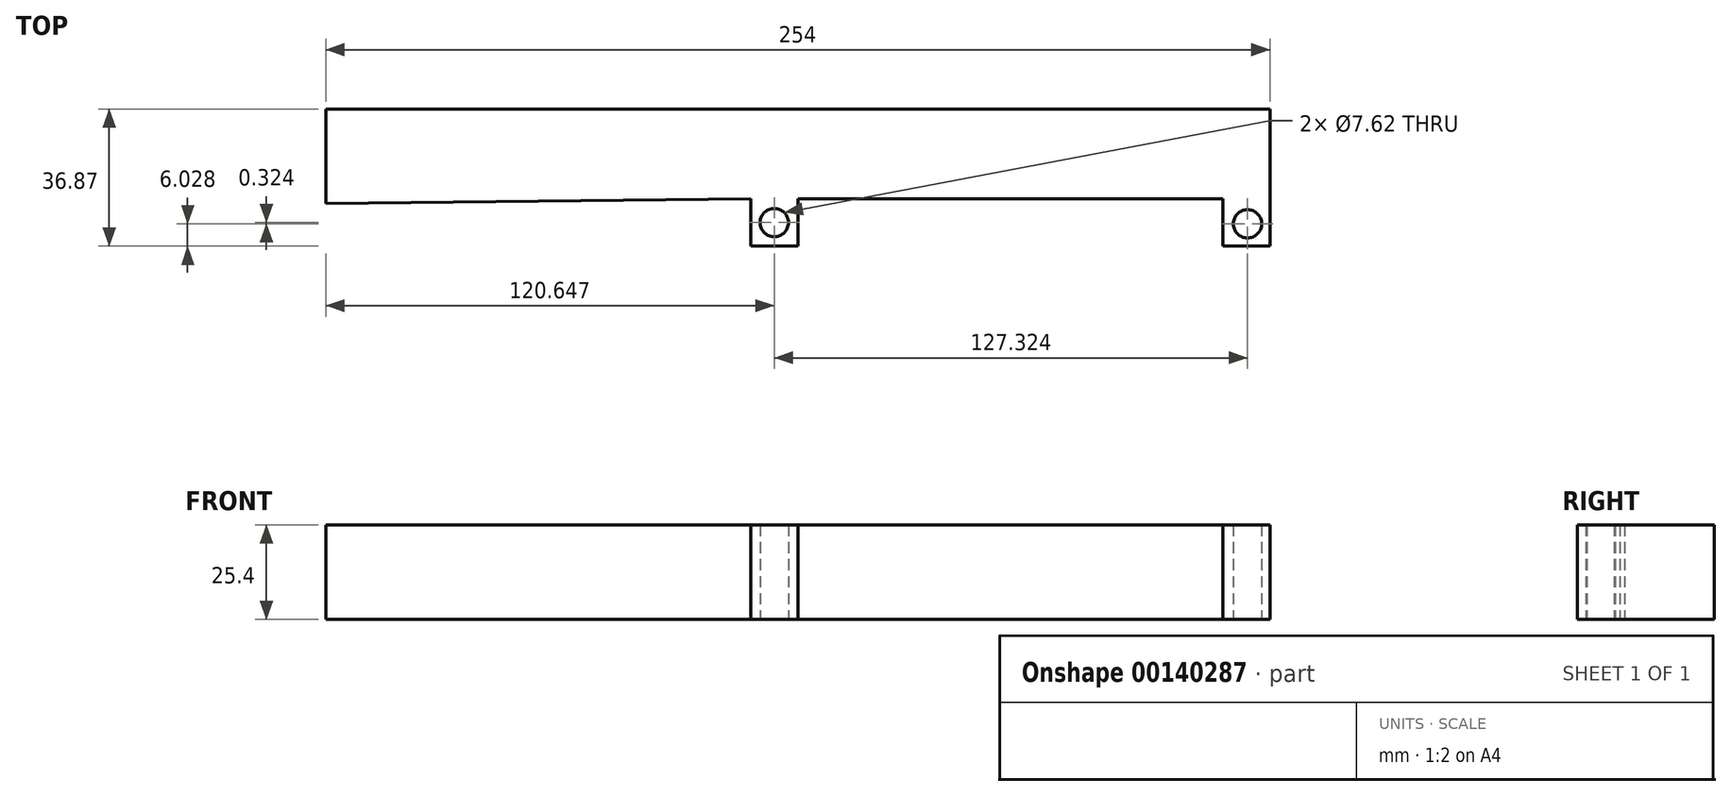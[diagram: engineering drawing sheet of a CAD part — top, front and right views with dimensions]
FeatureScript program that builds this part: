
annotation { "Feature Type Name" : "Feature", "Feature Type Description" : "" }
export const myFeature = defineFeature(function(context is Context, id is Id, definition is map)
    precondition{}
    {
        {
            var Q0;
            Q0=qCreatedBy(makeId("Top.planeOp"),FACE);
            var sketch = newSketch(context, id + "F0", { "sketchPlane" : qUnion([Q0])});
            skLineSegment(sketch, "E0.bottom", {"start": v(-370.92, 72.32) * mm, "end": v(-116.92, 72.32) * mm});
            skLineSegment(sketch, "E0.left", {"start": v(-370.92, 72.32) * mm, "end": v(-370.92, 46.92) * mm});
            skLineSegment(sketch, "E0.right", {"start": v(-116.92, 72.32) * mm, "end": v(-116.92, 46.92) * mm});
            skLineSegment(sketch, "E1.top", {"start": v(-116.92, 35.45) * mm, "end": v(-129.62, 35.45) * mm});
            skLineSegment(sketch, "E1.left", {"start": v(-116.92, 46.92) * mm, "end": v(-116.92, 35.45) * mm});
            skLineSegment(sketch, "E1.right", {"start": v(-129.62, 48.15) * mm, "end": v(-129.62, 35.45) * mm});
            skLineSegment(sketch, "E2", {"start": v(-129.62, 48.15) * mm, "end": v(-243.92, 48.15) * mm});
            skLineSegment(sketch, "E3.top", {"start": v(-243.92, 35.45) * mm, "end": v(-256.62, 35.45) * mm});
            skLineSegment(sketch, "E3.left", {"start": v(-243.92, 48.15) * mm, "end": v(-243.92, 35.45) * mm});
            skLineSegment(sketch, "E3.right", {"start": v(-256.62, 48.15) * mm, "end": v(-256.62, 35.45) * mm});
            skLineSegment(sketch, "E4", {"start": v(-256.62, 48.15) * mm, "end": v(-370.92, 46.92) * mm});
            skCircle(sketch, "E5", {"center": v(-250.27, 41.8) * mm, "radius": 3.81 * mm});
            skCircle(sketch, "E6", {"center": v(-122.95, 41.48) * mm, "radius": 3.81 * mm});
            skSolve(sketch);
        }
        {
            var Q0;
            Q0=makeQuery(id+"F0.imprint","IMPRINT",FACE,{"disambiguationData":[TD([[makeQuery(id+"F0.imprint","IMPRINT",EDGE,{"derivedFrom":sQuery(id+"F0.wireOp",EDGE,"E0.bottom")}),-1.0]])]});
            extrude(context, id + "F1", {"entities" : qUnion([Q0]), "depth" : 25.4 * mm});
        }
    });
